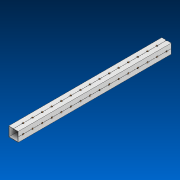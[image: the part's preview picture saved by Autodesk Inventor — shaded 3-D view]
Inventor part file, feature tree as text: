
AUTODESK INVENTOR PART (.ipt)
format: ipt  version: 2022.2 (Build 262287000, 287)  size: 792,064 bytes
history: native  units: in
note: dims shown in document units (in); Inventor stores cm internally (conversion verified against a paired STEP export)
features: other x32, pattern_linear x2, extrude x1, sketch x1
ambient origin geometry x8: Origin, YZ Plane, XZ Plane, XY Plane, X Axis, Y Axis, Z Axis, Center Point
bodies: Solid1 (feature_tree)
feature tree (36):
  extrude  "Extrusion1"  TaperAngle=0.0deg  [1 undecoded]
  other  "Work Axis1"
  other  "Work Axis2"
  pattern_linear  "Rectangular Pattern1"  Count1=16  [1 undecoded]
  pattern_linear  "Rectangular Pattern2"  Spacing1=1.0in  [1 undecoded]
  sketch  "Sketch1"  dims[d0=43.0in d1=0.0in d2=6.2992in d4=1.0in d5=5.9055in d7=1.0in]
  other  "Work Axis3"
  other  "Work Axis4"
  other  "Work Axis5"
  other  "Work Axis6"
  other  "Work Axis7"
  other  "Work Axis8"
  other  "Work Axis9"
  other  "Work Axis10"
  other  "Work Axis11"
  other  "Work Axis12"
  other  "Work Axis13"
  other  "Work Axis14"
  other  "Work Axis15"
  other  "Work Axis16"
  other  "Work Axis17"
  other  "Work Axis63"
  other  "Work Axis64"
  other  "Work Axis65"
  other  "Work Axis66"
  other  "Work Axis67"
  other  "Work Axis68"
  other  "Work Axis69"
  other  "Work Axis70"
  other  "Work Axis71"
  other  "Work Axis72"
  other  "Work Axis119"
  other  "Work Axis120"
  other  "Work Axis121"
  other  "Work Axis122"
  other  "LPattern2"
note: 3 required parameter values undecoded (feature->parameter linkage not recoverable at this tier; creation-order binding heuristic only, values carry confidence <= 0.55)
